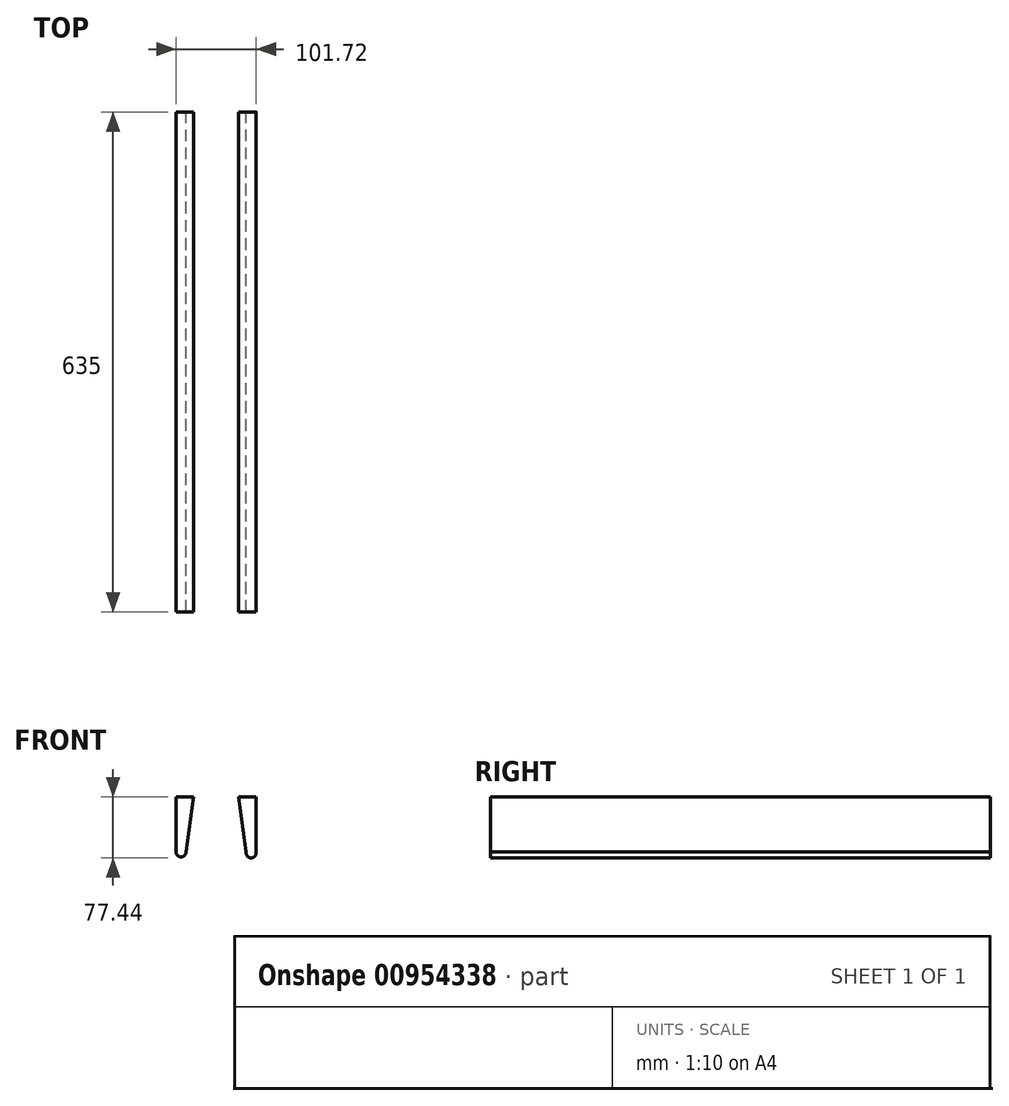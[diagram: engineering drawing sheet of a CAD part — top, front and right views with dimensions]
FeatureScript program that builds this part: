
annotation { "Feature Type Name" : "Feature", "Feature Type Description" : "" }
export const myFeature = defineFeature(function(context is Context, id is Id, definition is map)
    precondition{}
    {
        {
            var Q0;
            Q0=qCreatedBy(makeId("Front.planeOp"),FACE);
            var sketch = newSketch(context, id + "F0", { "sketchPlane" : qUnion([Q0])});
            skLineSegment(sketch, "E0.bottom", {"start": v(-47.76, 32.02) * mm, "end": v(53.84, 32.02) * mm});
            skLineSegment(sketch, "E0.top", {"start": v(-47.76, 38.37) * mm, "end": v(53.84, 38.37) * mm});
            skLineSegment(sketch, "E0.left", {"start": v(-47.76, 32.02) * mm, "end": v(-47.76, 38.37) * mm});
            skLineSegment(sketch, "E0.right", {"start": v(53.84, 32.02) * mm, "end": v(53.84, 38.37) * mm});
            skPoint(sketch, "E0.middle", {"position": v(3.04, 35.2) * mm});
            skLineSegment(sketch, "E1", {"start": v(-47.76, 38.37) * mm, "end": v(-47.76, -37.83) * mm});
            skLineSegment(sketch, "E2", {"start": v(53.84, 38.37) * mm, "end": v(53.84, -37.83) * mm});
            skArc(sketch, "E3", {"start": v(-47.76, -37.83) * mm, "mid": v(-41.4, -44.18) * mm, "end": v(-35.06, -37.83) * mm});
            skArc(sketch, "E4", {"start": v(41.38, -37.83) * mm, "mid": v(47.61, -45.42) * mm, "end": v(53.84, -37.83) * mm});
            skLineSegment(sketch, "E5", {"start": v(-35.06, -37.83) * mm, "end": v(-25.53, 32.02) * mm});
            skLineSegment(sketch, "E6", {"start": v(41.38, -37.83) * mm, "end": v(31.62, 32.02) * mm});
            skLineSegment(sketch, "E7", {"start": v(-25.53, 32.02) * mm, "end": v(31.62, 32.02) * mm});
            skLineSegment(sketch, "E8", {"start": v(-47.76, 32.02) * mm, "end": v(-25.53, 32.02) * mm});
            skLineSegment(sketch, "E9", {"start": v(53.84, 32.02) * mm, "end": v(31.62, 32.02) * mm});
            skLineSegment(sketch, "E10", {"start": v(53.84, 38.37) * mm, "end": v(53.84, 32.02) * mm});
            skLineSegment(sketch, "E11", {"start": v(3.04, 38.37) * mm, "end": v(3.04, 32.02) * mm});
            skSolve(sketch);
        }
        {
            var Q0;
            Q0=makeQuery(id+"F0.imprint","IMPRINT",FACE,{"disambiguationData":[TD([[makeQuery(id+"F0.imprint","IMPRINT",EDGE,{"derivedFrom":sQuery(id+"F0.wireOp",EDGE,"E2")}),-1.0]])]});
            var Q1;
            {var subQ1=sQuery(id+"F0.wireOp",EDGE,"E9");Q1=makeQuery(id+"F0.imprint","IMPRINT",FACE,{"disambiguationData":[TD([[makeQuery(id+"F0.imprint","IMPRINT",EDGE,{"derivedFrom":subQ1}),-1.0]])]});}
            var Q2;
            {var subQ0=sQuery(id+"F0.wireOp",EDGE,"E8");Q2=makeQuery(id+"F0.imprint","IMPRINT",FACE,{"disambiguationData":[TD([[makeQuery(id+"F0.imprint","IMPRINT",EDGE,{"derivedFrom":subQ0}),1.0]])]});}
            var Q3;
            {var subQ0=sQuery(id+"F0.wireOp",EDGE,"E3");Q3=makeQuery(id+"F0.imprint","IMPRINT",FACE,{"disambiguationData":[TD([[makeQuery(id+"F0.imprint","IMPRINT",EDGE,{"derivedFrom":subQ0}),1.0]])]});}
            extrude(context, id + "F1", {"entities" : qUnion([Q0, Q1, Q2, Q3]), "depth" : 635 * mm, "offsetDistance" : 25.4 * mm, "symmetric" : true});
        }
    });
